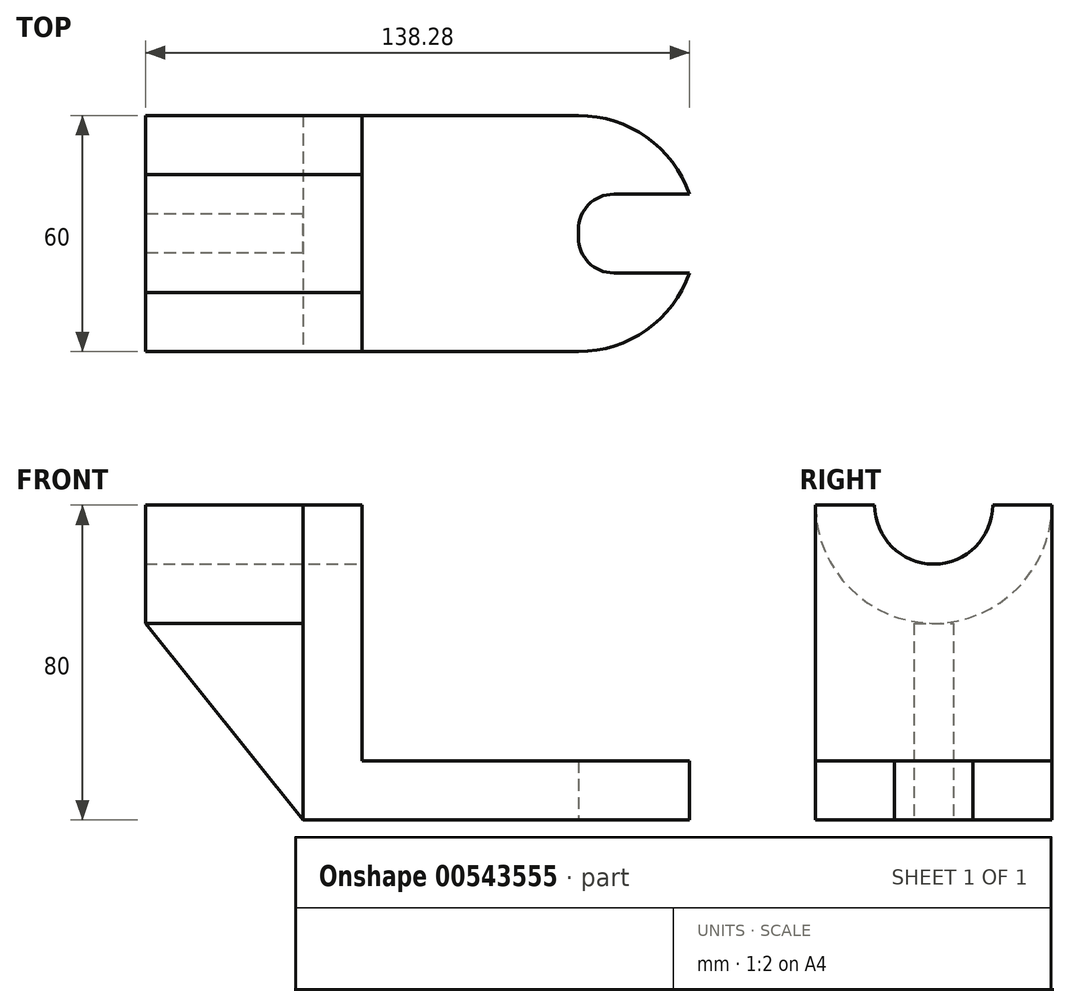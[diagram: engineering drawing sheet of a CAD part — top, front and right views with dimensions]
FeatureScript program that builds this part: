
annotation { "Feature Type Name" : "Feature", "Feature Type Description" : "" }
export const myFeature = defineFeature(function(context is Context, id is Id, definition is map)
    precondition{}
    {
        {
            var Q0;
            Q0=qCreatedBy(makeId("Top.planeOp"),FACE);
            var sketch = newSketch(context, id + "F0", { "sketchPlane" : qUnion([Q0])});
            skLineSegment(sketch, "E0.bottom", {"start": v(35, 30) * mm, "end": v(-35, 30) * mm});
            skLineSegment(sketch, "E0.top", {"start": v(35, -30) * mm, "end": v(-35, -30) * mm});
            skLineSegment(sketch, "E0.left", {"start": v(35, 30) * mm, "end": v(35, -30) * mm});
            skLineSegment(sketch, "E0.right", {"start": v(-35, 30) * mm, "end": v(-35, -30) * mm});
            skPoint(sketch, "E0.middle", {"position": v(0, 0) * mm});
            skArc(sketch, "E1", {"start": v(35, -30) * mm, "mid": v(65, 0) * mm, "end": v(35, 30) * mm});
            skLineSegment(sketch, "E2", {"start": v(65, 0) * mm, "end": v(65, 10) * mm});
            skLineSegment(sketch, "E3", {"start": v(65, 10) * mm, "end": v(65, -10) * mm});
            skLineSegment(sketch, "E4", {"start": v(65, 10) * mm, "end": v(35, 10) * mm});
            skLineSegment(sketch, "E5", {"start": v(65, -10) * mm, "end": v(35, -10) * mm});
            skSolve(sketch);
        }
        {
            var Q0;
            {var subQ4=sQuery(id+"F0.wireOp",EDGE,"E0.bottom");Q0=makeQuery(id+"F0.imprint","IMPRINT",FACE,{"disambiguationData":[TD([[makeQuery(id+"F0.imprint","IMPRINT",EDGE,{"derivedFrom":subQ4}),1.0]])]});}
            var Q1;
            {var subQ1=sQuery(id+"F0.wireOp",EDGE,"E0.left");var subQ3=sQuery(id+"F0.wireOp",EDGE,"E4");var subQ4=makeQuery(id+"F0.imprint","INTERSECT",VERTEX,{"derivedFrom":[subQ1,subQ3]});Q1=makeQuery(id+"F0.imprint","IMPRINT",FACE,{"disambiguationData":[TD([[makeQuery(id+"F0.imprint","IMPRINT",EDGE,{"disambiguationData":[TD([[subQ4,1.0]])],"derivedFrom":subQ3}),-1.0]])]});}
            var Q2;
            {var subQ1=sQuery(id+"F0.wireOp",EDGE,"E0.left");var subQ3=sQuery(id+"F0.wireOp",EDGE,"E5");var subQ4=makeQuery(id+"F0.imprint","INTERSECT",VERTEX,{"derivedFrom":[subQ1,subQ3]});Q2=makeQuery(id+"F0.imprint","IMPRINT",FACE,{"disambiguationData":[TD([[makeQuery(id+"F0.imprint","IMPRINT",EDGE,{"disambiguationData":[TD([[subQ4,1.0]])],"derivedFrom":subQ3}),1.0]])]});}
            extrude(context, id + "F1", {"entities" : qUnion([Q0, Q1, Q2]), "depth" : 15 * mm, "offsetDistance" : 25 * mm});
        }
        {
            var Q0;
            Q0=qCreatedBy(makeId("Front.planeOp"),FACE);
            var sketch = newSketch(context, id + "F2", { "sketchPlane" : qUnion([Q0])});
            skLineSegment(sketch, "E6.0.0", {"start": v(-35, 0) * mm, "end": v(35, 0) * mm});
            skLineSegment(sketch, "E6.0.1", {"start": v(35, 0) * mm, "end": v(35, 15) * mm});
            skLineSegment(sketch, "E6.0.2", {"start": v(35, 15) * mm, "end": v(-35, 15) * mm});
            skLineSegment(sketch, "E6.0.3", {"start": v(-35, 15) * mm, "end": v(-35, 0) * mm});
            skLineSegment(sketch, "E7", {"start": v(-35, 15) * mm, "end": v(-35, 80) * mm});
            skLineSegment(sketch, "E8", {"start": v(-35, 80) * mm, "end": v(-20, 80) * mm});
            skLineSegment(sketch, "E9", {"start": v(-20, 80) * mm, "end": v(-20, 15) * mm});
            skSolve(sketch);
        }
        {
            var Q0;
            Q0 = qSketchRegion(id + "F2", true);
            extrude(context, id + "F3", {"entities" : qUnion([Q0]), "operationType" : NewBodyOperationType.ADD, "depth" : 30 * mm, "offsetDistance" : 25 * mm, "hasSecondDirection" : true, "secondDirectionOppositeDirection" : true, "secondDirectionDepth" : 30 * mm});
        }
        {
            var Q0;
            Q0=makeQuery(id+"F3.boolean.opBoolean","MERGE",FACE,{"derivedFrom":[makeQuery(id+"F1.opExtrude","SWEPT_FACE",FACE,{"disambiguationData":[OSD([sQuery(id+"F0.wireOp",EDGE,"E0.right")])]}),makeQuery(id+"F3.opExtrude","SWEPT_FACE",FACE,{"disambiguationData":[OSD([sQuery(id+"F2.wireOp",EDGE,"E6.0.3"),sQuery(id+"F2.wireOp",EDGE,"E7")])]})]});
            var sketch = newSketch(context, id + "F4", { "sketchPlane" : qUnion([Q0])});
            skArc(sketch, "E10", {"start": v(-15, 80) * mm, "mid": v(0, 65) * mm, "end": v(15, 80) * mm});
            skArc(sketch, "E11", {"start": v(-30, 80) * mm, "mid": v(0, 50) * mm, "end": v(30, 80) * mm});
            skLineSegment(sketch, "E12", {"start": v(30, 80) * mm, "end": v(15, 80) * mm});
            skLineSegment(sketch, "E13.trimOffspring", {"start": v(-15, 80) * mm, "end": v(-30, 80) * mm});
            skSolve(sketch);
        }
        {
            var Q0;
            Q0 = qSketchRegion(id + "F4", true);
            extrude(context, id + "F5", {"entities" : qUnion([Q0]), "operationType" : NewBodyOperationType.ADD, "depth" : 40 * mm, "offsetDistance" : 25 * mm});
        }
        {
            var Q0;
            Q0=makeQuery(id+"F5.boolean.opBoolean","SPLIT",FACE,{"disambiguationData":[TD([makeQuery(id+"F5.opExtrude","SWEPT_FACE",FACE,{"disambiguationData":[OSD([sQuery(id+"F4.wireOp",EDGE,"E10")])]})])],"derivedFrom":makeQuery(id+"F3.boolean.opBoolean","MERGE",FACE,{"derivedFrom":[makeQuery(id+"F1.opExtrude","SWEPT_FACE",FACE,{"disambiguationData":[OSD([sQuery(id+"F0.wireOp",EDGE,"E0.right")])]}),makeQuery(id+"F3.opExtrude","SWEPT_FACE",FACE,{"disambiguationData":[OSD([sQuery(id+"F2.wireOp",EDGE,"E6.0.3"),sQuery(id+"F2.wireOp",EDGE,"E7")])]})]})});
            extrude(context, id + "F6", {"entities" : qUnion([Q0]), "operationType" : NewBodyOperationType.REMOVE, "oppositeDirection" : true, "depth" : 25 * mm, "offsetDistance" : 25 * mm});
        }
        {
            var Q0;
            Q0=qCreatedBy(makeId("Front.planeOp"),FACE);
            var sketch = newSketch(context, id + "F7", { "sketchPlane" : qUnion([Q0])});
            skLineSegment(sketch, "E14", {"start": v(-35, 50) * mm, "end": v(-75, 50) * mm});
            skLineSegment(sketch, "E15.0.0", {"start": v(-35, 0) * mm, "end": v(35, 0) * mm});
            skLineSegment(sketch, "E15.0.1", {"start": v(35, 0) * mm, "end": v(35, 15) * mm});
            skLineSegment(sketch, "E15.0.2", {"start": v(35, 15) * mm, "end": v(-20, 15) * mm});
            skLineSegment(sketch, "E15.0.3", {"start": v(-20, 15) * mm, "end": v(-20, 80) * mm});
            skLineSegment(sketch, "E15.0.4", {"start": v(-20, 80) * mm, "end": v(-35, 80) * mm});
            skLineSegment(sketch, "E15.0.5", {"start": v(-35, 80) * mm, "end": v(-35, 0) * mm});
            skLineSegment(sketch, "E16", {"start": v(-75, 50) * mm, "end": v(-35, 0) * mm});
            skSolve(sketch);
        }
        {
            var Q0;
            {var subQ0=sQuery(id+"F7.wireOp",EDGE,"E14");Q0=makeQuery(id+"F7.imprint","IMPRINT",FACE,{"disambiguationData":[TD([[makeQuery(id+"F7.imprint","IMPRINT",EDGE,{"derivedFrom":subQ0}),1.0]])]});}
            extrude(context, id + "F8", {"entities" : qUnion([Q0]), "depth" : 5 * mm, "offsetDistance" : 25 * mm, "hasSecondDirection" : true, "secondDirectionOppositeDirection" : true, "secondDirectionDepth" : 5 * mm});
        }
        {
            var Q0;
            Q0=makeQuery(id+"F1.opExtrude","SWEPT_EDGE",EDGE,{"disambiguationData":[OSD([sQuery(id+"F0.wireOp",EDGE,"E0.left"),sQuery(id+"F0.wireOp",EDGE,"E4")])]});
            var Q1;
            Q1=makeQuery(id+"F1.opExtrude","SWEPT_EDGE",EDGE,{"disambiguationData":[OSD([sQuery(id+"F0.wireOp",EDGE,"E0.left"),sQuery(id+"F0.wireOp",EDGE,"E5")])]});
            fillet(context, id + "F9", {"entities" : qUnion([Q0, Q1]), "radius" : 9 * mm, "tangentPropagation" : true, "allowEdgeOverflow" : false});
        }
    });
